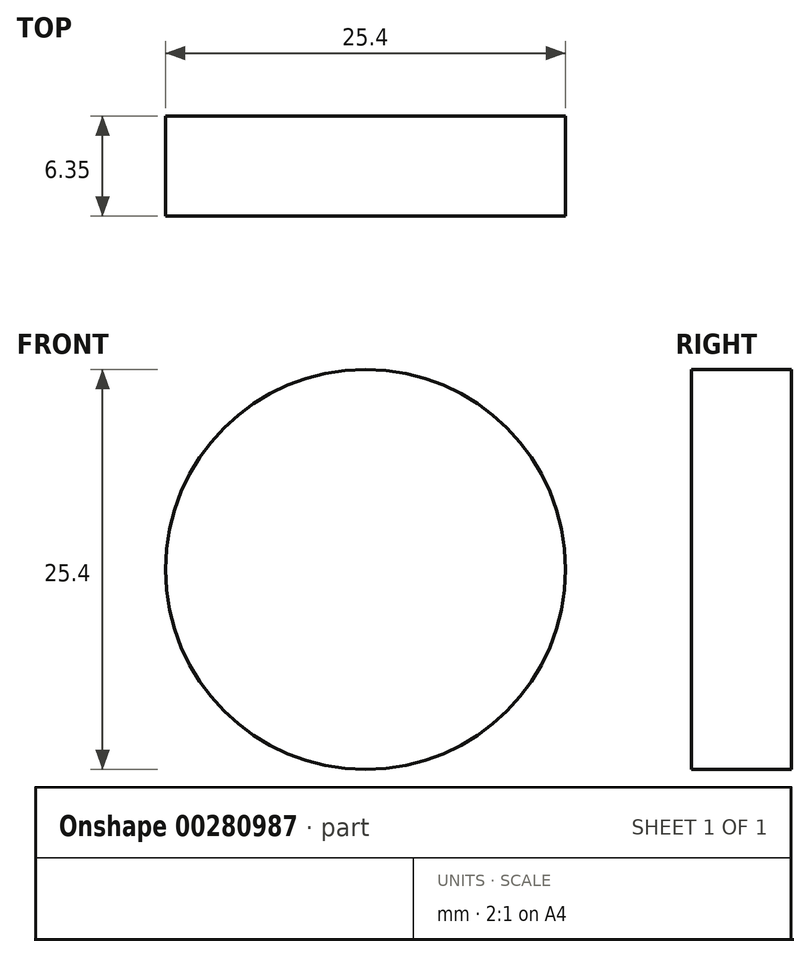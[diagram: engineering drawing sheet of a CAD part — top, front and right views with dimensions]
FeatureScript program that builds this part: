
annotation { "Feature Type Name" : "Feature", "Feature Type Description" : "" }
export const myFeature = defineFeature(function(context is Context, id is Id, definition is map)
    precondition{}
    {
        {
            var Q0;
            Q0=qCreatedBy(makeId("Front.planeOp"),FACE);
            var sketch = newSketch(context, id + "F0", { "sketchPlane" : qUnion([Q0])});
            skCircle(sketch, "E0", {"center": v(0, 0) * mm, "radius": 12.7 * mm});
            skSolve(sketch);
        }
        {
            var Q0;
            Q0=makeQuery(id+"F0.imprint","IMPRINT",FACE,{"disambiguationData":[TD([[makeQuery(id+"F0.imprint","IMPRINT",EDGE,{"derivedFrom":sQuery(id+"F0.wireOp",EDGE,"E0")}),1.0]])]});
            extrude(context, id + "F1", {"entities" : qUnion([Q0]), "depth" : 6.35 * mm});
        }
    });
